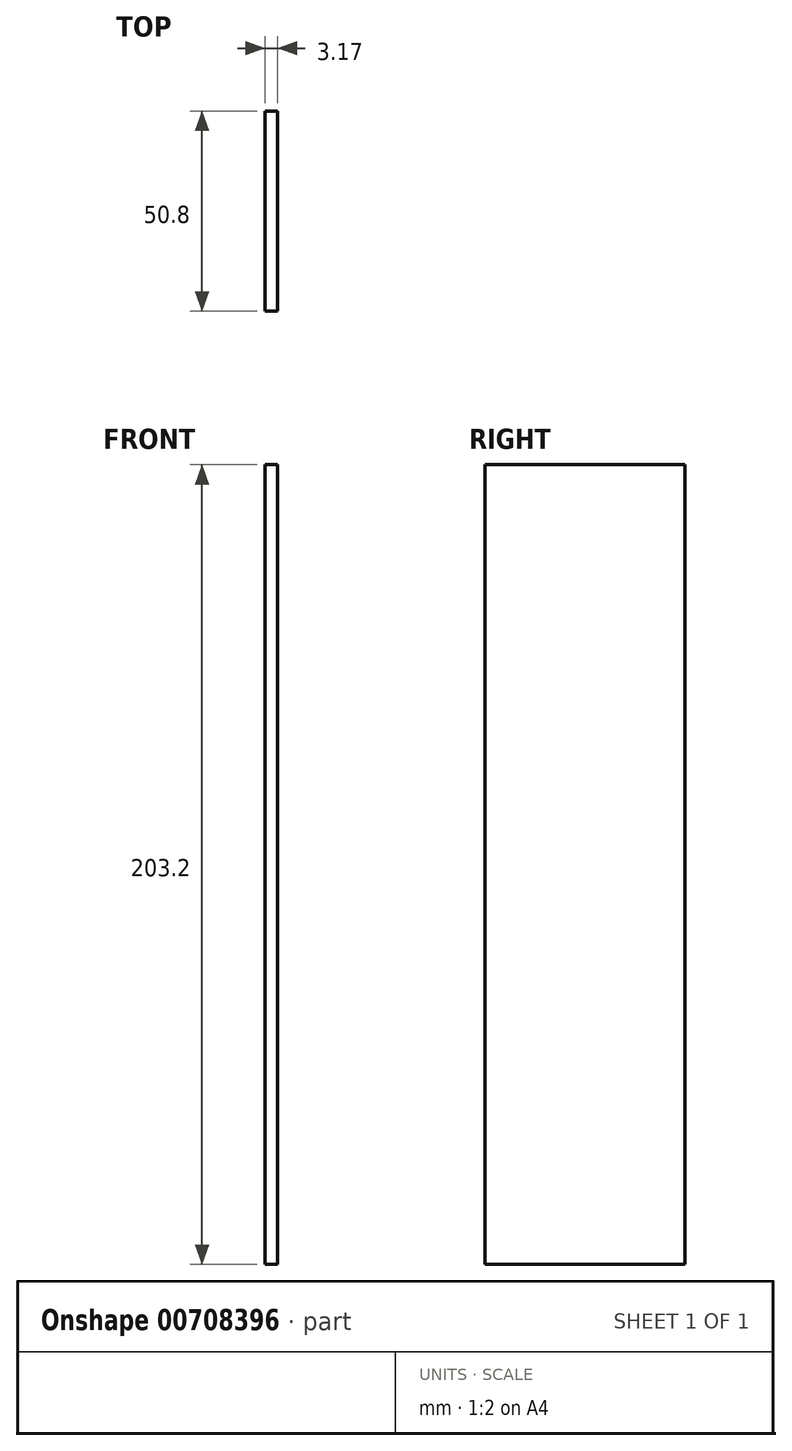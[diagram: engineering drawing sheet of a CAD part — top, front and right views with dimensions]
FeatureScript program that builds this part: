
annotation { "Feature Type Name" : "Feature", "Feature Type Description" : "" }
export const myFeature = defineFeature(function(context is Context, id is Id, definition is map)
    precondition{}
    {
        {
            var Q0;
            Q0=qCreatedBy(makeId("Right.planeOp"),FACE);
            var sketch = newSketch(context, id + "F0", { "sketchPlane" : qUnion([Q0])});
            skLineSegment(sketch, "E0", {"start": v(0, 0) * mm, "end": v(0, 203.2) * mm});
            skLineSegment(sketch, "E1", {"start": v(0, 203.2) * mm, "end": v(50.8, 203.2) * mm});
            skLineSegment(sketch, "E2", {"start": v(50.8, 203.2) * mm, "end": v(50.8, 0) * mm});
            skLineSegment(sketch, "E3", {"start": v(50.8, 0) * mm, "end": v(0, 0) * mm});
            skSolve(sketch);
        }
        {
            var Q0;
            Q0=makeQuery(id+"F0.imprint","IMPRINT",FACE,{"disambiguationData":[TD([[makeQuery(id+"F0.imprint","IMPRINT",EDGE,{"derivedFrom":sQuery(id+"F0.wireOp",EDGE,"E0")}),-1.0]])]});
            extrude(context, id + "F1", {"entities" : qUnion([Q0]), "oppositeDirection" : true, "depth" : 3.17 * mm, "offsetDistance" : 25.4 * mm});
        }
    });
